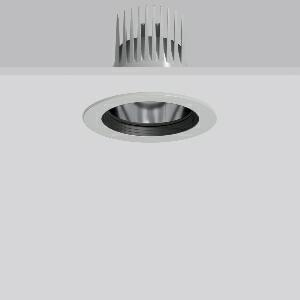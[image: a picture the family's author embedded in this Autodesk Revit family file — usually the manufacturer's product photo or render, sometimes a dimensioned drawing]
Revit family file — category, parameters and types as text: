
# Revit family: heledon_maxi_e_901759_004_1_c827
name_source: partatom
category: Lighting Fixtures
units: mm (PartAtom-declared; Revit-internal decimal feet)

## family parameters
Cut with Voids When Loaded = No
Host = Face
Light Source = No
Part Type = Normal
Room Calculation Point = No
Round Connector Dimension = Use Diameter
Shared = No

## types (1)
- HELEDON maxi E (1 x LED Modul 940, 3350 lm, 4000)
    Apparent Load = 25 VA
    Approval mark = CE
    CIE Flux Codes = 97 100 100 100 100
    Color Rendering = 92
    Color Temperature = 4000
    Default Elevation = 1800 mm
    Description = Series: HELEDON maxi
Round recessed downlight. Housing: die-cast aluminium, powder-coated. Black plastic ring and recessed LED to prevent glare from the side. Optical assembly with reflector made of MIRO-Silver with 98% total light reflection for outstanding efficiency - can be changed without tools. Best colour rendering index Ra>90. Suitable for Recessed ceiling mounting. Installation without tools thanks to spring fastening system. Including separate LED converter with connecting cable 600 mm.High quality converter without flickering and stroboscopic effect. Through-wiring box (5 pole) available as accessory. The following accessories can be mounted without use of tools: interchangeable lenses, decorative glasses, honeycomb louvre, clear and frosted diffusers, white interchangeable plastic ring. 
Colour: silver
Diameter: 162 mm
Height: 3 mm
Cut-out diameter: 152 mm
Recess height: 200 mm
Luminaire: recess height: 135 mm
Lamp: LED
Socket: without socket
Colour temperature: 4000K
Colour rendering index (CRI): 92
System power: 25 W
Rated luminous flux: 3350 lm
Luminous efficiency: 134 lm/W
Control gear: Regulated power supply
Protection class: II
Type of protection: IP 20
    Height = 0 mm  [stored 0 ft]
    Lamp = 1 x LED Modul 940
    Lamp Light Flux = 3350 lm
    Lamp count = 1
    Length = 162 mm
    Lifetime = 50000 h
    Luminous efficacy = 134 lm/W
    Manufacturer = RZB
    ModVariant = No
    Model = 901759.004.1
    Mounting Place = Ceiling
    Mounting Type = Recessed
    Number of Poles = 1
    OnlyDefault = Yes
    Power Factor = 1
    Product Name = HELEDON maxi E
    Product group = Recessed downlights
    ProductGroupID = 402
    Protection Class = Protection class II
    Protection Degree = IP 20
    RLX_Detail_Level = 1
    RLX_Emergency_Light_Flux = 0 lm
    RLX_Emergency_Type = 0
    RLX_Emergency_Type_DB = No
    RlxData = <blob elided: 119533 chars, md5=5abc9ec3>
    Socket = socket
    Standby Power = 0 W
    System Light Flux = 3350 lm
    System Power = 25 W
    Type Comments = Product without accessories
    Type Image = 901662.004.jpg
    URL = http://relux.com
    VarID = ---
    Voltage = 230 V
    Voltage Range = 220-240 V
    Weight = 0.00 kg
    Width = 0 mm  [stored 0 ft]

note: [stored X ft] marks values corroborated as IEEE doubles in the binary element streams (Revit-internal decimal feet)

## geometry (parser evidence)
native form markers: Blend x4, Sweep x10
no freeform markers — native parametric forms only
